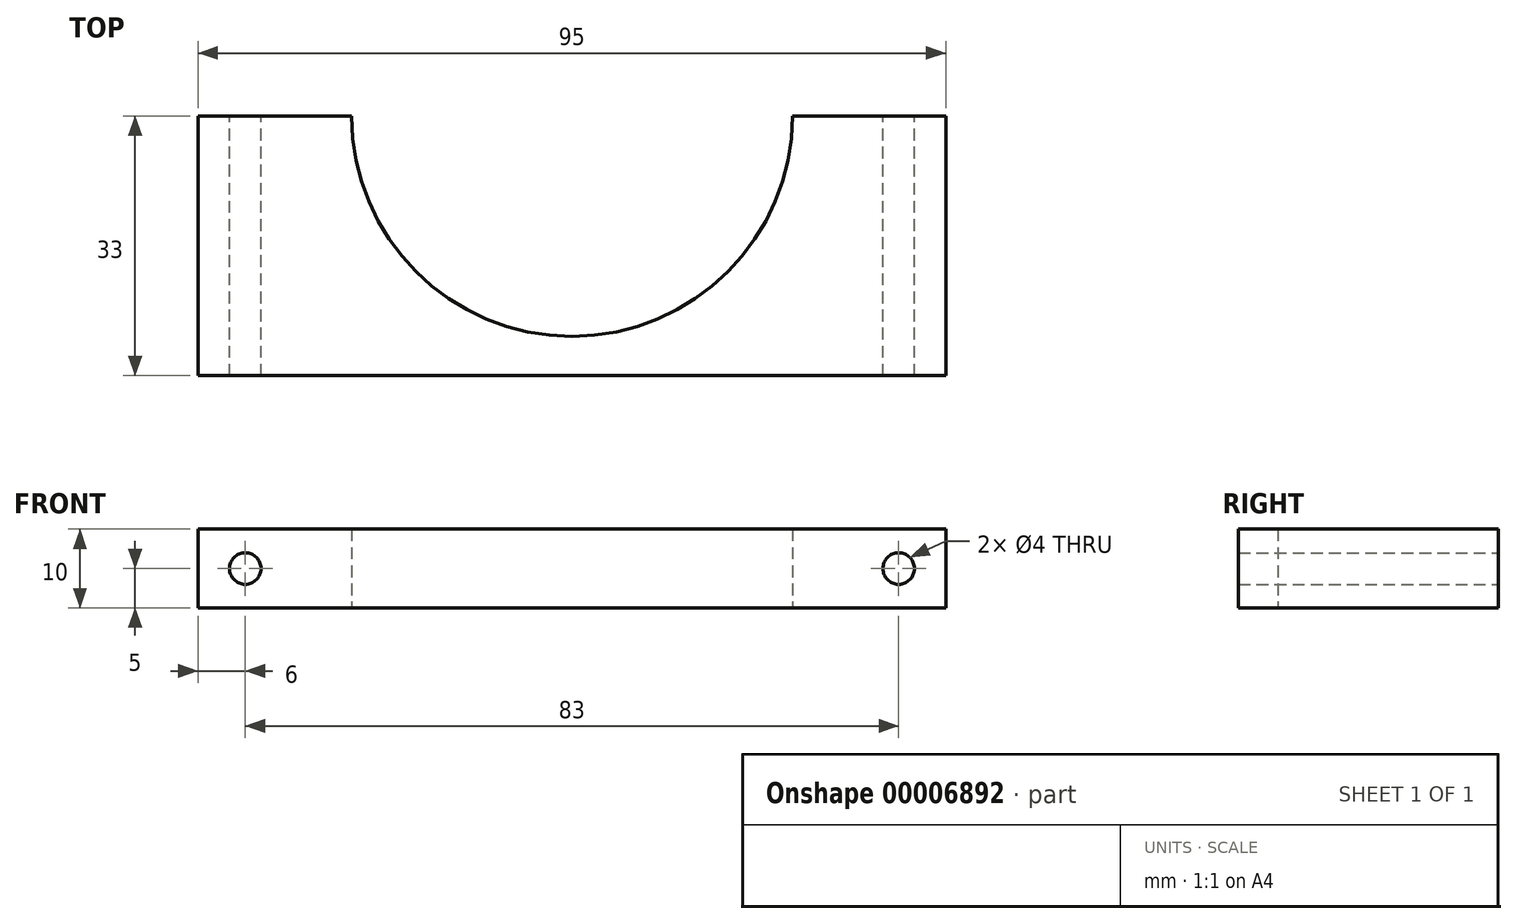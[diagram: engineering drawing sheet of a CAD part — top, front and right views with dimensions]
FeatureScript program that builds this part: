
annotation { "Feature Type Name" : "Feature", "Feature Type Description" : "" }
export const myFeature = defineFeature(function(context is Context, id is Id, definition is map)
    precondition{}
    {
        {
            var Q0;
            Q0=qCreatedBy(makeId("Top.planeOp"),FACE);
            var sketch = newSketch(context, id + "F0", { "sketchPlane" : qUnion([Q0])});
            skLineSegment(sketch, "E0.bottom", {"start": v(-47.5, -6.56) * mm, "end": v(-28, -6.56) * mm});
            skLineSegment(sketch, "E0.top", {"start": v(-47.5, -39.56) * mm, "end": v(47.5, -39.56) * mm});
            skLineSegment(sketch, "E0.left", {"start": v(-47.5, -6.56) * mm, "end": v(-47.5, -39.56) * mm});
            skLineSegment(sketch, "E0.right", {"start": v(47.5, -6.56) * mm, "end": v(47.5, -39.56) * mm});
            skArc(sketch, "E1", {"start": v(-28, -6.56) * mm, "mid": v(0, -34.56) * mm, "end": v(28, -6.56) * mm});
            skLineSegment(sketch, "E2.trimOffspring", {"start": v(28, -6.56) * mm, "end": v(47.5, -6.56) * mm});
            skSolve(sketch);
        }
        {
            var Q0;
            Q0=qSketchRegion(id+"F0",true);
            var Q1;
            Q1=makeQuery(id+"F0.imprint","IMPRINT",FACE,{"disambiguationData":[TD([[makeQuery(id+"F0.imprint","IMPRINT",EDGE,{"derivedFrom":sQuery(id+"F0.wireOp",EDGE,"E0.bottom")}),-1.0]])]});
            extrude(context, id + "F1", {"entities" : qUnion([Q0, Q1]), "depth" : 10 * mm});
        }
        {
            var Q0;
            Q0=makeQuery(id+"F1.opExtrude","SWEPT_FACE",FACE,{"disambiguationData":[OSD([sQuery(id+"F0.wireOp",EDGE,"E2.trimOffspring")])]});
            var sketch = newSketch(context, id + "F2", { "sketchPlane" : qUnion([Q0])});
            skLineSegment(sketch, "E3", {"start": v(-41.5, 10) * mm, "end": v(-41.5, 0) * mm, "construction": true});
            skLineSegment(sketch, "E4", {"start": v(-47.5, 5) * mm, "end": v(-28, 5) * mm, "construction": true});
            skCircle(sketch, "E5", {"center": v(-41.5, 5) * mm, "radius": 2 * mm});
            skSolve(sketch);
        }
        {
            var Q0;
            Q0=qSketchRegion(id+"F2",true);
            extrude(context, id + "F3", {"entities" : qUnion([Q0]), "operationType" : NewBodyOperationType.REMOVE, "endBound" : BoundingType.THROUGH_ALL, "oppositeDirection" : true, "depth" : 25 * mm});
        }
        {
            var Q0;
            Q0=makeQuery(id+"F1.opExtrude","SWEPT_FACE",FACE,{"disambiguationData":[OSD([sQuery(id+"F0.wireOp",EDGE,"E0.bottom")])]});
            var sketch = newSketch(context, id + "F4", { "sketchPlane" : qUnion([Q0])});
            skLineSegment(sketch, "E6", {"start": v(41.5, 10) * mm, "end": v(41.5, 0) * mm, "construction": true});
            skLineSegment(sketch, "E7", {"start": v(47.5, 5) * mm, "end": v(28, 5) * mm, "construction": true});
            skCircle(sketch, "E8", {"center": v(41.5, 5) * mm, "radius": 2 * mm});
            skSolve(sketch);
        }
        {
            var Q0;
            Q0=qSketchRegion(id+"F4",true);
            extrude(context, id + "F5", {"entities" : qUnion([Q0]), "operationType" : NewBodyOperationType.REMOVE, "endBound" : BoundingType.THROUGH_ALL, "oppositeDirection" : true, "depth" : 25 * mm});
        }
    });
